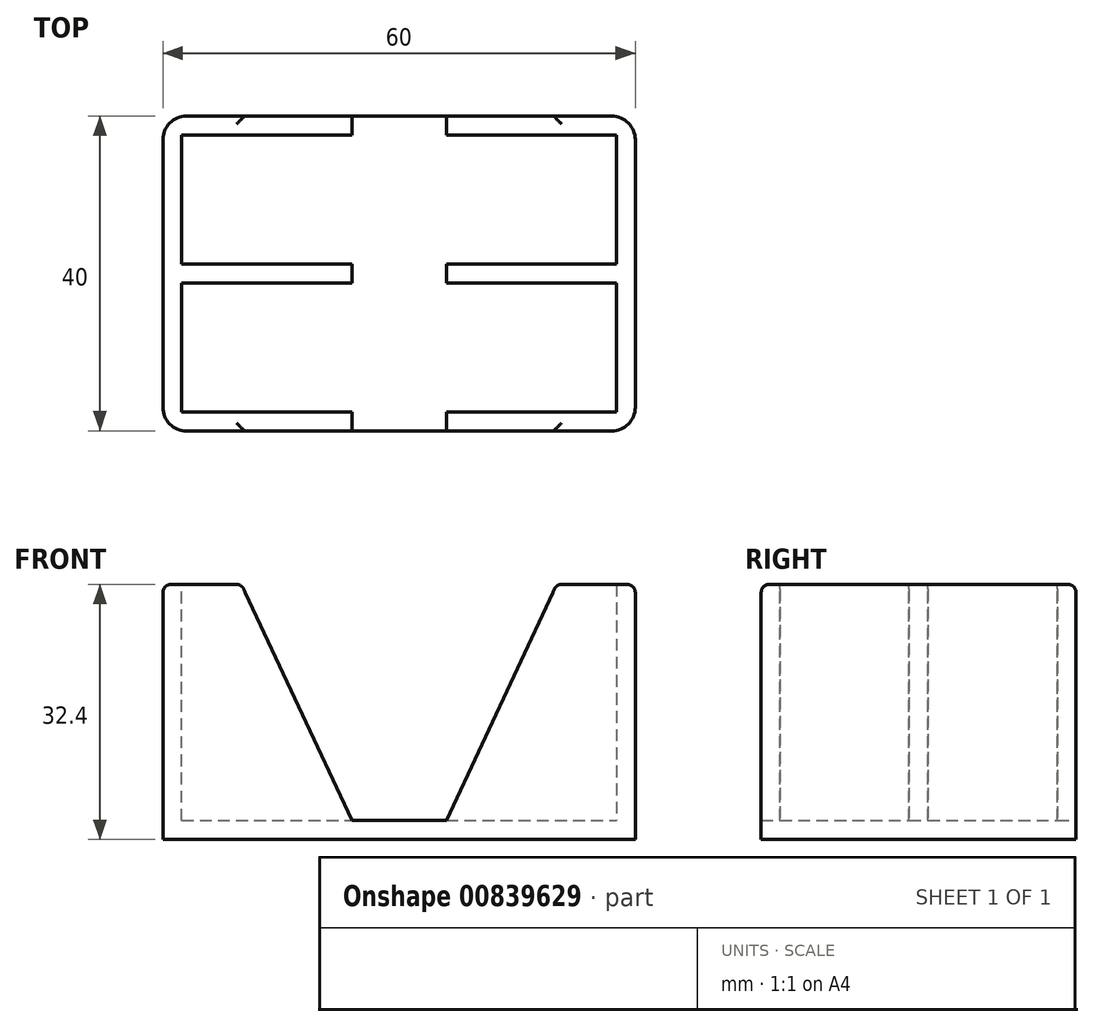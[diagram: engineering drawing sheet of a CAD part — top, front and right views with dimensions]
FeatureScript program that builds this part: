
annotation { "Feature Type Name" : "Feature", "Feature Type Description" : "" }
export const myFeature = defineFeature(function(context is Context, id is Id, definition is map)
    precondition{}
    {
        {
            var Q0;
            Q0=qCreatedBy(makeId("Top.planeOp"),FACE);
            var sketch = newSketch(context, id + "F0", { "sketchPlane" : qUnion([Q0])});
            skLineSegment(sketch, "E0.bottom", {"start": v(30, -20) * mm, "end": v(-30, -20) * mm});
            skLineSegment(sketch, "E0.top", {"start": v(30, 20) * mm, "end": v(-30, 20) * mm});
            skLineSegment(sketch, "E0.left", {"start": v(30, -20) * mm, "end": v(30, 20) * mm});
            skLineSegment(sketch, "E0.right", {"start": v(-30, -20) * mm, "end": v(-30, 20) * mm});
            skPoint(sketch, "E0.middle", {"position": v(0, 0) * mm});
            skSolve(sketch);
        }
        {
            var Q0;
            Q0 = qSketchRegion(id + "F0", true);
            extrude(context, id + "F1", {"entities" : qUnion([Q0]), "oppositeDirection" : true, "depth" : 2.4 * mm, "offsetDistance" : 25 * mm});
        }
        {
            var Q0;
            Q0=qCreatedBy(makeId("Front.planeOp"),FACE);
            var sketch = newSketch(context, id + "F2", { "sketchPlane" : qUnion([Q0])});
            skLineSegment(sketch, "E1", {"start": v(-30, 0) * mm, "end": v(-30, 30) * mm});
            skLineSegment(sketch, "E2", {"start": v(-30, 30) * mm, "end": v(-20, 30) * mm});
            skLineSegment(sketch, "E3", {"start": v(-20, 30) * mm, "end": v(-6, 0) * mm});
            skLineSegment(sketch, "E4.MirrorCS", {"start": v(30, 0) * mm, "end": v(30, 30) * mm});
            skLineSegment(sketch, "E5.MirrorCS", {"start": v(30, 30) * mm, "end": v(20, 30) * mm});
            skLineSegment(sketch, "E6.MirrorCS", {"start": v(20, 30) * mm, "end": v(6, 0) * mm});
            skLineSegment(sketch, "E7", {"start": v(-30, 0) * mm, "end": v(-6, 0) * mm});
            skLineSegment(sketch, "E8", {"start": v(6, 0) * mm, "end": v(30, 0) * mm});
            skSolve(sketch);
        }
        {
            var Q0;
            Q0 = qSketchRegion(id + "F2", true);
            extrude(context, id + "F3", {"entities" : qUnion([Q0]), "endBound" : BoundingType.SYMMETRIC, "depth" : 2.4 * mm, "offsetDistance" : 25 * mm});
        }
        {
            var Q0;
            Q0=makeQuery(id+"F3.opExtrude","SWEPT_BODY",BODY,{"disambiguationData":[OSD([sQuery(id+"F2.wireOp",EDGE,"E1"),sQuery(id+"F2.wireOp",EDGE,"E2"),sQuery(id+"F2.wireOp",EDGE,"E3"),sQuery(id+"F2.wireOp",EDGE,"E7")])]});
            transform(context, id + "F4", {"entities" : qUnion([Q0]), "transformType" : TransformType.TRANSLATION_3D, "dx" : 0 * mm, "dy" : 18.8 * mm, "dz" : 0 * mm, "makeCopy" : true});
        }
        {
            var Q0;
            Q0=makeQuery(id+"F3.opExtrude","SWEPT_BODY",BODY,{"disambiguationData":[OSD([sQuery(id+"F2.wireOp",EDGE,"E1"),sQuery(id+"F2.wireOp",EDGE,"E2"),sQuery(id+"F2.wireOp",EDGE,"E3"),sQuery(id+"F2.wireOp",EDGE,"E7")])]});
            transform(context, id + "F5", {"entities" : qUnion([Q0]), "transformType" : TransformType.TRANSLATION_3D, "dx" : 0 * mm, "dy" : -18.8 * mm, "dz" : 0 * mm, "makeCopy" : true});
        }
        {
            var Q0;
            Q0=makeQuery(id+"F3.opExtrude","SWEPT_BODY",BODY,{"disambiguationData":[OSD([sQuery(id+"F2.wireOp",EDGE,"E4.MirrorCS"),sQuery(id+"F2.wireOp",EDGE,"E5.MirrorCS"),sQuery(id+"F2.wireOp",EDGE,"E6.MirrorCS"),sQuery(id+"F2.wireOp",EDGE,"E8")])]});
            transform(context, id + "F6", {"entities" : qUnion([Q0]), "transformType" : TransformType.TRANSLATION_3D, "dx" : 0 * mm, "dy" : 18.8 * mm, "dz" : 0 * mm, "makeCopy" : true});
        }
        {
            var Q0;
            Q0=makeQuery(id+"F3.opExtrude","SWEPT_BODY",BODY,{"disambiguationData":[OSD([sQuery(id+"F2.wireOp",EDGE,"E4.MirrorCS"),sQuery(id+"F2.wireOp",EDGE,"E5.MirrorCS"),sQuery(id+"F2.wireOp",EDGE,"E6.MirrorCS"),sQuery(id+"F2.wireOp",EDGE,"E8")])]});
            transform(context, id + "F7", {"entities" : qUnion([Q0]), "transformType" : TransformType.TRANSLATION_3D, "dx" : 0 * mm, "dy" : -18.8 * mm, "dz" : 0 * mm, "makeCopy" : true});
        }
        {
            var Q0;
            Q0=makeQuery(id+"F3.opExtrude","SWEPT_BODY",BODY,{"disambiguationData":[OSD([sQuery(id+"F2.wireOp",EDGE,"E1"),sQuery(id+"F2.wireOp",EDGE,"E2"),sQuery(id+"F2.wireOp",EDGE,"E3"),sQuery(id+"F2.wireOp",EDGE,"E7")])]});
            var Q1;
            Q1=makeQuery(id+"F5.opPattern","COPY",BODY,{"derivedFrom":makeQuery(id+"F3.opExtrude","SWEPT_BODY",BODY,{"disambiguationData":[OSD([sQuery(id+"F2.wireOp",EDGE,"E1"),sQuery(id+"F2.wireOp",EDGE,"E2"),sQuery(id+"F2.wireOp",EDGE,"E3"),sQuery(id+"F2.wireOp",EDGE,"E7")])]}),"instanceName":"1"});
            var Q2;
            Q2=makeQuery(id+"F4.opPattern","COPY",BODY,{"derivedFrom":makeQuery(id+"F3.opExtrude","SWEPT_BODY",BODY,{"disambiguationData":[OSD([sQuery(id+"F2.wireOp",EDGE,"E1"),sQuery(id+"F2.wireOp",EDGE,"E2"),sQuery(id+"F2.wireOp",EDGE,"E3"),sQuery(id+"F2.wireOp",EDGE,"E7")])]}),"instanceName":"1"});
            transform(context, id + "F8", {"entities" : qUnion([Q0, Q1, Q2]), "transformType" : TransformType.TRANSLATION_3D, "dx" : 2.4 * mm, "dy" : 0 * mm, "dz" : 0 * mm, "makeCopy" : true});
        }
        {
            var Q0;
            Q0=makeQuery(id+"F8.opPattern","COPY",BODY,{"derivedFrom":makeQuery(id+"F3.opExtrude","SWEPT_BODY",BODY,{"disambiguationData":[OSD([sQuery(id+"F2.wireOp",EDGE,"E1"),sQuery(id+"F2.wireOp",EDGE,"E2"),sQuery(id+"F2.wireOp",EDGE,"E3"),sQuery(id+"F2.wireOp",EDGE,"E7")])]}),"instanceName":"1"});
            deleteBodies(context, id + "F9", {"entities" : qUnion([Q0])});
        }
        {
            var Q0;
            Q0=makeQuery(id+"F8.opPattern","COPY",BODY,{"derivedFrom":makeQuery(id+"F4.opPattern","COPY",BODY,{"derivedFrom":makeQuery(id+"F3.opExtrude","SWEPT_BODY",BODY,{"disambiguationData":[OSD([sQuery(id+"F2.wireOp",EDGE,"E1"),sQuery(id+"F2.wireOp",EDGE,"E2"),sQuery(id+"F2.wireOp",EDGE,"E3"),sQuery(id+"F2.wireOp",EDGE,"E7")])]}),"instanceName":"1"}),"instanceName":"1"});
            deleteBodies(context, id + "F10", {"entities" : qUnion([Q0])});
        }
        {
            var Q0;
            Q0=makeQuery(id+"F8.opPattern","COPY",BODY,{"derivedFrom":makeQuery(id+"F5.opPattern","COPY",BODY,{"derivedFrom":makeQuery(id+"F3.opExtrude","SWEPT_BODY",BODY,{"disambiguationData":[OSD([sQuery(id+"F2.wireOp",EDGE,"E1"),sQuery(id+"F2.wireOp",EDGE,"E2"),sQuery(id+"F2.wireOp",EDGE,"E3"),sQuery(id+"F2.wireOp",EDGE,"E7")])]}),"instanceName":"1"}),"instanceName":"1"});
            deleteBodies(context, id + "F11", {"entities" : qUnion([Q0])});
        }
        {
            var Q0;
            Q0=makeQuery(id+"F1.opExtrude","CAP_FACE",FACE,{"disambiguationData":[OSD([sQuery(id+"F0.wireOp",EDGE,"E0.bottom"),sQuery(id+"F0.wireOp",EDGE,"E0.top"),sQuery(id+"F0.wireOp",EDGE,"E0.left"),sQuery(id+"F0.wireOp",EDGE,"E0.right")])],"isStart":true});
            var sketch = newSketch(context, id + "F12", { "sketchPlane" : qUnion([Q0])});
            skLineSegment(sketch, "E9.0", {"start": v(27.6, -17.6) * mm, "end": v(27.6, 17.6) * mm});
            skLineSegment(sketch, "E9.1", {"start": v(-27.6, -17.6) * mm, "end": v(27.6, -17.6) * mm});
            skLineSegment(sketch, "E9.2", {"start": v(-27.6, 17.6) * mm, "end": v(-27.6, -17.6) * mm});
            skLineSegment(sketch, "E9.3", {"start": v(27.6, 17.6) * mm, "end": v(-27.6, 17.6) * mm});
            skLineSegment(sketch, "E10", {"start": v(27.6, -17.6) * mm, "end": v(27.6, -20) * mm});
            skLineSegment(sketch, "E11", {"start": v(-27.6, -17.6) * mm, "end": v(-27.6, -20) * mm});
            skLineSegment(sketch, "E12", {"start": v(-27.6, 17.6) * mm, "end": v(-27.6, 20) * mm});
            skLineSegment(sketch, "E13", {"start": v(27.6, 17.6) * mm, "end": v(27.6, 20) * mm});
            skSolve(sketch);
        }
        {
            var Q0;
            Q0=makeQuery(id+"F12.imprint","IMPRINT",FACE,{"disambiguationData":[TD([[makeQuery(id+"F12.imprint","IMPRINT",EDGE,{"derivedFrom":sQuery(id+"F12.wireOp",EDGE,"E9.0")}),-1.0]])]});
            var Q1;
            Q1=makeQuery(id+"F12.imprint","IMPRINT",FACE,{"disambiguationData":[TD([[makeQuery(id+"F12.imprint","IMPRINT",EDGE,{"derivedFrom":sQuery(id+"F12.wireOp",EDGE,"E9.2")}),-1.0]])]});
            extrude(context, id + "F13", {"entities" : qUnion([Q0, Q1]), "operationType" : NewBodyOperationType.ADD, "depth" : 30 * mm, "offsetDistance" : 25 * mm});
        }
        {
            var Q0;
            Q0=makeQuery(id+"F13.boolean.opBoolean","MERGE",EDGE,{"derivedFrom":[makeQuery(id+"F1.opExtrude","SWEPT_EDGE",EDGE,{"disambiguationData":[OSD([sQuery(id+"F0.wireOp",EDGE,"E0.bottom"),sQuery(id+"F0.wireOp",EDGE,"E0.left")])]}),makeQuery(id+"F7.opPattern","COPY",EDGE,{"derivedFrom":makeQuery(id+"F3.opExtrude","CAP_EDGE",EDGE,{"disambiguationData":[OSD([sQuery(id+"F2.wireOp",EDGE,"E4.MirrorCS")])],"isStart":false}),"instanceName":"1"})]});
            var Q1;
            Q1=makeQuery(id+"F13.boolean.opBoolean","MERGE",EDGE,{"derivedFrom":[makeQuery(id+"F1.opExtrude","SWEPT_EDGE",EDGE,{"disambiguationData":[OSD([sQuery(id+"F0.wireOp",EDGE,"E0.bottom"),sQuery(id+"F0.wireOp",EDGE,"E0.right")])]}),makeQuery(id+"F5.opPattern","COPY",EDGE,{"derivedFrom":makeQuery(id+"F3.opExtrude","CAP_EDGE",EDGE,{"disambiguationData":[OSD([sQuery(id+"F2.wireOp",EDGE,"E1")])],"isStart":false}),"instanceName":"1"})]});
            var Q2;
            Q2=makeQuery(id+"F13.boolean.opBoolean","MERGE",EDGE,{"derivedFrom":[makeQuery(id+"F1.opExtrude","SWEPT_EDGE",EDGE,{"disambiguationData":[OSD([sQuery(id+"F0.wireOp",EDGE,"E0.top"),sQuery(id+"F0.wireOp",EDGE,"E0.right")])]}),makeQuery(id+"F4.opPattern","COPY",EDGE,{"derivedFrom":makeQuery(id+"F3.opExtrude","CAP_EDGE",EDGE,{"disambiguationData":[OSD([sQuery(id+"F2.wireOp",EDGE,"E1")])],"isStart":true}),"instanceName":"1"})]});
            var Q3;
            Q3=makeQuery(id+"F13.boolean.opBoolean","MERGE",EDGE,{"derivedFrom":[makeQuery(id+"F1.opExtrude","SWEPT_EDGE",EDGE,{"disambiguationData":[OSD([sQuery(id+"F0.wireOp",EDGE,"E0.top"),sQuery(id+"F0.wireOp",EDGE,"E0.left")])]}),makeQuery(id+"F6.opPattern","COPY",EDGE,{"derivedFrom":makeQuery(id+"F3.opExtrude","CAP_EDGE",EDGE,{"disambiguationData":[OSD([sQuery(id+"F2.wireOp",EDGE,"E4.MirrorCS")])],"isStart":true}),"instanceName":"1"})]});
            fillet(context, id + "F14", {"entities" : qUnion([Q0, Q1, Q2, Q3]), "radius" : 3 * mm, "tangentPropagation" : true, "allowEdgeOverflow" : false});
        }
        {
            var Q0;
            Q0=makeQuery(id+"F6.opPattern","COPY",EDGE,{"derivedFrom":makeQuery(id+"F3.opExtrude","SWEPT_EDGE",EDGE,{"disambiguationData":[OSD([sQuery(id+"F2.wireOp",EDGE,"E5.MirrorCS"),sQuery(id+"F2.wireOp",EDGE,"E6.MirrorCS")])]}),"instanceName":"1"});
            var Q1;
            Q1=makeQuery(id+"F3.opExtrude","SWEPT_EDGE",EDGE,{"disambiguationData":[OSD([sQuery(id+"F2.wireOp",EDGE,"E5.MirrorCS"),sQuery(id+"F2.wireOp",EDGE,"E6.MirrorCS")])]});
            var Q2;
            Q2=makeQuery(id+"F7.opPattern","COPY",EDGE,{"derivedFrom":makeQuery(id+"F3.opExtrude","SWEPT_EDGE",EDGE,{"disambiguationData":[OSD([sQuery(id+"F2.wireOp",EDGE,"E5.MirrorCS"),sQuery(id+"F2.wireOp",EDGE,"E6.MirrorCS")])]}),"instanceName":"1"});
            var Q3;
            Q3=makeQuery(id+"F6.opPattern","COPY",EDGE,{"derivedFrom":makeQuery(id+"F3.opExtrude","SWEPT_EDGE",EDGE,{"disambiguationData":[OSD([sQuery(id+"F2.wireOp",EDGE,"E6.MirrorCS"),sQuery(id+"F2.wireOp",EDGE,"E8")])]}),"instanceName":"1"});
            var Q4;
            Q4=makeQuery(id+"F3.opExtrude","SWEPT_EDGE",EDGE,{"disambiguationData":[OSD([sQuery(id+"F2.wireOp",EDGE,"E6.MirrorCS"),sQuery(id+"F2.wireOp",EDGE,"E8")])]});
            var Q5;
            Q5=makeQuery(id+"F7.opPattern","COPY",EDGE,{"derivedFrom":makeQuery(id+"F3.opExtrude","SWEPT_EDGE",EDGE,{"disambiguationData":[OSD([sQuery(id+"F2.wireOp",EDGE,"E6.MirrorCS"),sQuery(id+"F2.wireOp",EDGE,"E8")])]}),"instanceName":"1"});
            var Q6;
            Q6=makeQuery(id+"F4.opPattern","COPY",EDGE,{"derivedFrom":makeQuery(id+"F3.opExtrude","SWEPT_EDGE",EDGE,{"disambiguationData":[OSD([sQuery(id+"F2.wireOp",EDGE,"E2"),sQuery(id+"F2.wireOp",EDGE,"E3")])]}),"instanceName":"1"});
            var Q7;
            Q7=makeQuery(id+"F3.opExtrude","SWEPT_EDGE",EDGE,{"disambiguationData":[OSD([sQuery(id+"F2.wireOp",EDGE,"E2"),sQuery(id+"F2.wireOp",EDGE,"E3")])]});
            var Q8;
            Q8=makeQuery(id+"F5.opPattern","COPY",EDGE,{"derivedFrom":makeQuery(id+"F3.opExtrude","SWEPT_EDGE",EDGE,{"disambiguationData":[OSD([sQuery(id+"F2.wireOp",EDGE,"E2"),sQuery(id+"F2.wireOp",EDGE,"E3")])]}),"instanceName":"1"});
            var Q9;
            Q9=makeQuery(id+"F5.opPattern","COPY",EDGE,{"derivedFrom":makeQuery(id+"F3.opExtrude","SWEPT_EDGE",EDGE,{"disambiguationData":[OSD([sQuery(id+"F2.wireOp",EDGE,"E3"),sQuery(id+"F2.wireOp",EDGE,"E7")])]}),"instanceName":"1"});
            var Q10;
            Q10=makeQuery(id+"F3.opExtrude","SWEPT_EDGE",EDGE,{"disambiguationData":[OSD([sQuery(id+"F2.wireOp",EDGE,"E3"),sQuery(id+"F2.wireOp",EDGE,"E7")])]});
            var Q11;
            Q11=makeQuery(id+"F4.opPattern","COPY",EDGE,{"derivedFrom":makeQuery(id+"F3.opExtrude","SWEPT_EDGE",EDGE,{"disambiguationData":[OSD([sQuery(id+"F2.wireOp",EDGE,"E3"),sQuery(id+"F2.wireOp",EDGE,"E7")])]}),"instanceName":"1"});
            var Q12;
            {var subQ0=makeQuery(id+"F3.opExtrude","SWEPT_EDGE",EDGE,{"disambiguationData":[OSD([sQuery(id+"F2.wireOp",EDGE,"E4.MirrorCS"),sQuery(id+"F2.wireOp",EDGE,"E5.MirrorCS")])]});Q12=makeQuery(id+"F13.boolean.opBoolean","MERGE",EDGE,{"derivedFrom":[subQ0,makeQuery(id+"F6.opPattern","COPY",EDGE,{"derivedFrom":subQ0,"instanceName":"1"}),makeQuery(id+"F7.opPattern","COPY",EDGE,{"derivedFrom":subQ0,"instanceName":"1"}),makeQuery(id+"F13.opExtrude","CAP_EDGE",EDGE,{"disambiguationData":[OSD([sQuery(id+"F0.wireOp",EDGE,"E0.left")])],"isStart":false})]});}
            var Q13;
            {var subQ0=makeQuery(id+"F3.opExtrude","SWEPT_EDGE",EDGE,{"disambiguationData":[OSD([sQuery(id+"F2.wireOp",EDGE,"E1"),sQuery(id+"F2.wireOp",EDGE,"E2")])]});Q13=makeQuery(id+"F13.boolean.opBoolean","MERGE",EDGE,{"derivedFrom":[subQ0,makeQuery(id+"F4.opPattern","COPY",EDGE,{"derivedFrom":subQ0,"instanceName":"1"}),makeQuery(id+"F5.opPattern","COPY",EDGE,{"derivedFrom":subQ0,"instanceName":"1"}),makeQuery(id+"F13.opExtrude","CAP_EDGE",EDGE,{"disambiguationData":[OSD([sQuery(id+"F0.wireOp",EDGE,"E0.right")])],"isStart":false})]});}
            fillet(context, id + "F15", {"entities" : qUnion([Q0, Q1, Q2, Q3, Q4, Q5, Q6, Q7, Q8, Q9, Q10, Q11, Q12, Q13]), "radius" : 1 * mm, "tangentPropagation" : true, "allowEdgeOverflow" : false});
        }
    });
